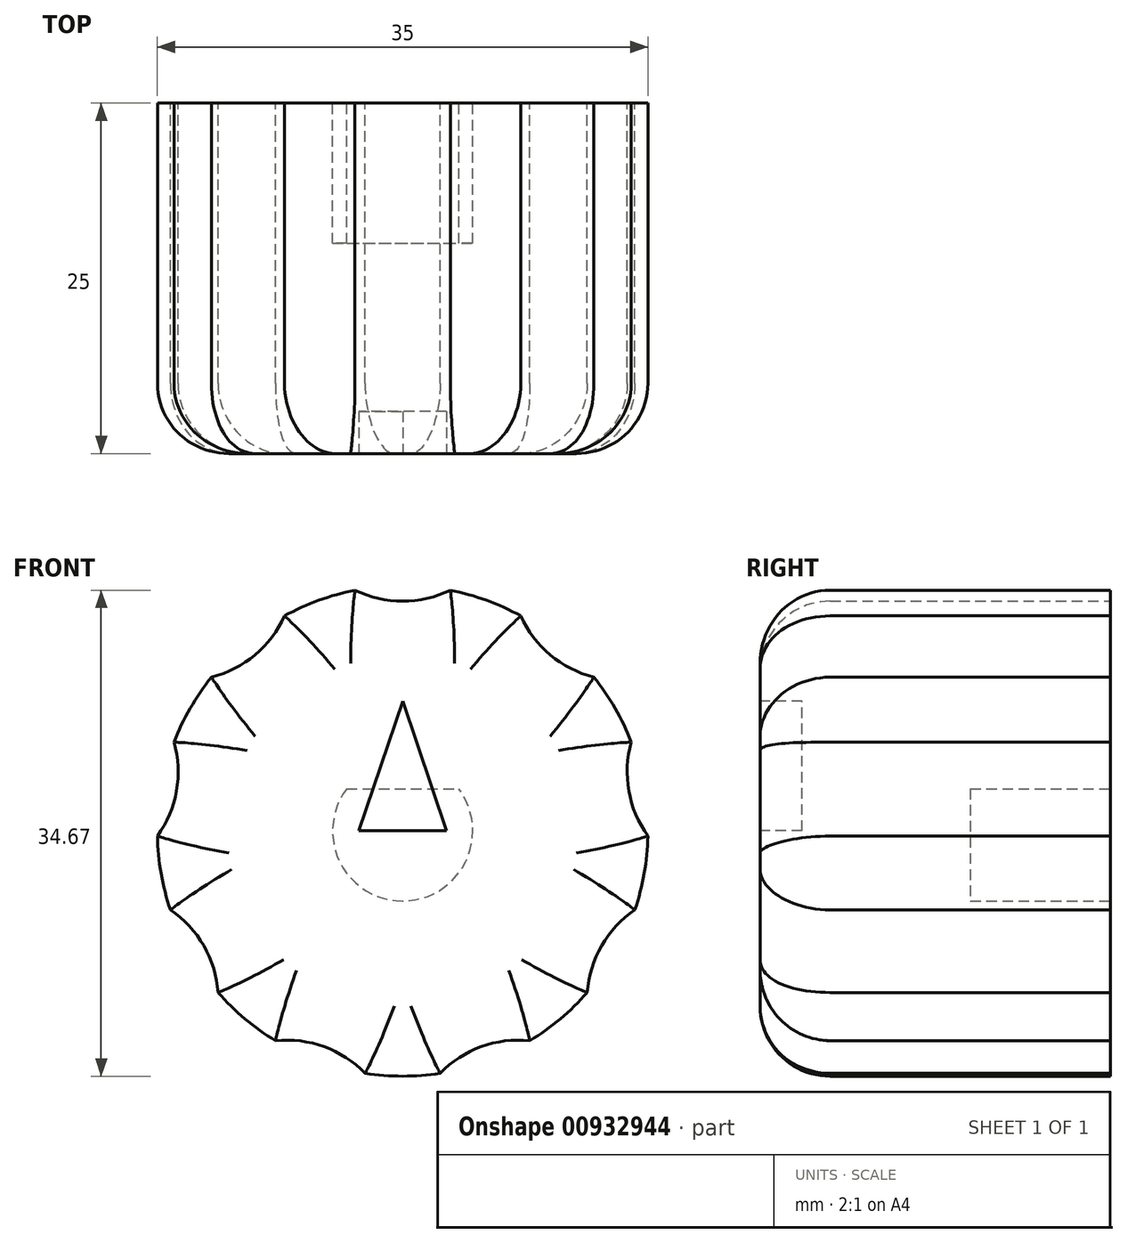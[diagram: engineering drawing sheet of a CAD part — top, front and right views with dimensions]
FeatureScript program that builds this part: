
annotation { "Feature Type Name" : "Feature", "Feature Type Description" : "" }
export const myFeature = defineFeature(function(context is Context, id is Id, definition is map)
    precondition{}
    {
        {
            var Q0;
            Q0=qCreatedBy(makeId("Front.planeOp"),FACE);
            var sketch = newSketch(context, id + "F0", { "sketchPlane" : qUnion([Q0])});
            skCircle(sketch, "E0", {"center": v(0, 0) * mm, "radius": 17.5 * mm});
            skCircle(sketch, "E1", {"center": v(0, 0) * mm, "radius": 5 * mm});
            skLineSegment(sketch, "E2", {"start": v(-4, 3) * mm, "end": v(4, 3) * mm});
            skArc(sketch, "E3", {"start": v(-3.4, 17.17) * mm, "mid": v(0, 16.39) * mm, "end": v(3.4, 17.17) * mm});
            skArc(sketch, "E4.1.0", {"start": v(-13.64, 10.96) * mm, "mid": v(-10.53, 12.55) * mm, "end": v(-8.43, 15.34) * mm});
            skArc(sketch, "E4.2.0", {"start": v(-17.5, -0.37) * mm, "mid": v(-16.14, 2.85) * mm, "end": v(-16.32, 6.33) * mm});
            skArc(sketch, "E4.3.0", {"start": v(-13.17, -11.53) * mm, "mid": v(-14.2, -8.2) * mm, "end": v(-16.57, -5.64) * mm});
            skArc(sketch, "E4.4.0", {"start": v(-2.68, -17.3) * mm, "mid": v(-5.6, -15.4) * mm, "end": v(-9.07, -14.97) * mm});
            skArc(sketch, "E4.5.0", {"start": v(9.07, -14.97) * mm, "mid": v(5.6, -15.4) * mm, "end": v(2.68, -17.3) * mm});
            skArc(sketch, "E4.6.0", {"start": v(16.57, -5.64) * mm, "mid": v(14.2, -8.2) * mm, "end": v(13.17, -11.53) * mm});
            skArc(sketch, "E4.7.0", {"start": v(16.32, 6.33) * mm, "mid": v(16.14, 2.85) * mm, "end": v(17.5, -0.37) * mm});
            skArc(sketch, "E4.8.0", {"start": v(8.43, 15.34) * mm, "mid": v(10.53, 12.55) * mm, "end": v(13.64, 10.96) * mm});
            skSolve(sketch);
        }
        {
            var Q0;
            {var subQ12=sQuery(id+"F0.wireOp",EDGE,"E3");Q0=makeQuery(id+"F0.imprint","IMPRINT",FACE,{"disambiguationData":[TD([[makeQuery(id+"F0.imprint","IMPRINT",EDGE,{"derivedFrom":subQ12}),-1.0]])]});}
            var Q1;
            {var subQ0=sQuery(id+"F0.wireOp",EDGE,"E2");Q1=makeQuery(id+"F0.imprint","IMPRINT",FACE,{"disambiguationData":[TD([[makeQuery(id+"F0.imprint","IMPRINT",EDGE,{"derivedFrom":subQ0}),-1.0]])]});}
            var Q2;
            {var subQ0=sQuery(id+"F0.wireOp",EDGE,"E2");Q2=makeQuery(id+"F0.imprint","IMPRINT",FACE,{"disambiguationData":[TD([[makeQuery(id+"F0.imprint","IMPRINT",EDGE,{"derivedFrom":subQ0}),1.0]])]});}
            extrude(context, id + "F1", {"entities" : qUnion([Q0, Q1, Q2]), "depth" : 25 * mm, "offsetDistance" : 25 * mm});
        }
        {
            var Q0;
            {var subQ0=sQuery(id+"F0.wireOp",EDGE,"E2");Q0=makeQuery(id+"F0.imprint","IMPRINT",FACE,{"disambiguationData":[TD([[makeQuery(id+"F0.imprint","IMPRINT",EDGE,{"derivedFrom":subQ0}),-1.0]])]});}
            extrude(context, id + "F2", {"entities" : qUnion([Q0]), "operationType" : NewBodyOperationType.REMOVE, "depth" : 10 * mm, "offsetDistance" : 25 * mm});
        }
        {
            var Q0;
            Q0=makeQuery(id+"F1.opExtrude","CAP_FACE",FACE,{"disambiguationData":[OSD([sQuery(id+"F0.wireOp",EDGE,"E0"),sQuery(id+"F0.wireOp",EDGE,"E3"),sQuery(id+"F0.wireOp",EDGE,"E4.1.0"),sQuery(id+"F0.wireOp",EDGE,"E4.2.0"),sQuery(id+"F0.wireOp",EDGE,"E4.3.0"),sQuery(id+"F0.wireOp",EDGE,"E4.4.0"),sQuery(id+"F0.wireOp",EDGE,"E4.5.0"),sQuery(id+"F0.wireOp",EDGE,"E4.6.0"),sQuery(id+"F0.wireOp",EDGE,"E4.7.0"),sQuery(id+"F0.wireOp",EDGE,"E4.8.0")])],"isStart":false});
            fillet(context, id + "F3", {"entities" : qUnion([Q0]), "radius" : 5 * mm, "tangentPropagation" : true, "allowEdgeOverflow" : false});
        }
        {
            var Q0;
            Q0=makeQuery(id+"F1.opExtrude","CAP_FACE",FACE,{"disambiguationData":[OSD([sQuery(id+"F0.wireOp",EDGE,"E0"),sQuery(id+"F0.wireOp",EDGE,"E3"),sQuery(id+"F0.wireOp",EDGE,"E4.1.0"),sQuery(id+"F0.wireOp",EDGE,"E4.2.0"),sQuery(id+"F0.wireOp",EDGE,"E4.3.0"),sQuery(id+"F0.wireOp",EDGE,"E4.4.0"),sQuery(id+"F0.wireOp",EDGE,"E4.5.0"),sQuery(id+"F0.wireOp",EDGE,"E4.6.0"),sQuery(id+"F0.wireOp",EDGE,"E4.7.0"),sQuery(id+"F0.wireOp",EDGE,"E4.8.0")])],"isStart":false});
            var sketch = newSketch(context, id + "F4", { "sketchPlane" : qUnion([Q0])});
            skLineSegment(sketch, "E5", {"start": v(0, 0) * mm, "end": v(3.12, 0) * mm});
            skLineSegment(sketch, "E6", {"start": v(3.12, 0) * mm, "end": v(0, 9.25) * mm});
            skLineSegment(sketch, "E7.MirrorCS", {"start": v(0, 0) * mm, "end": v(-3.12, 0) * mm});
            skLineSegment(sketch, "E8.MirrorCS", {"start": v(-3.12, 0) * mm, "end": v(0, 9.25) * mm});
            skSolve(sketch);
        }
        {
            var Q0;
            Q0=makeQuery(id+"F4.imprint","IMPRINT",FACE,{"disambiguationData":[TD([[makeQuery(id+"F4.imprint","IMPRINT",EDGE,{"derivedFrom":sQuery(id+"F4.wireOp",EDGE,"E5")}),1.0]])]});
            extrude(context, id + "F5", {"entities" : qUnion([Q0]), "operationType" : NewBodyOperationType.REMOVE, "oppositeDirection" : true, "depth" : 3 * mm, "offsetDistance" : 25 * mm});
        }
    });
